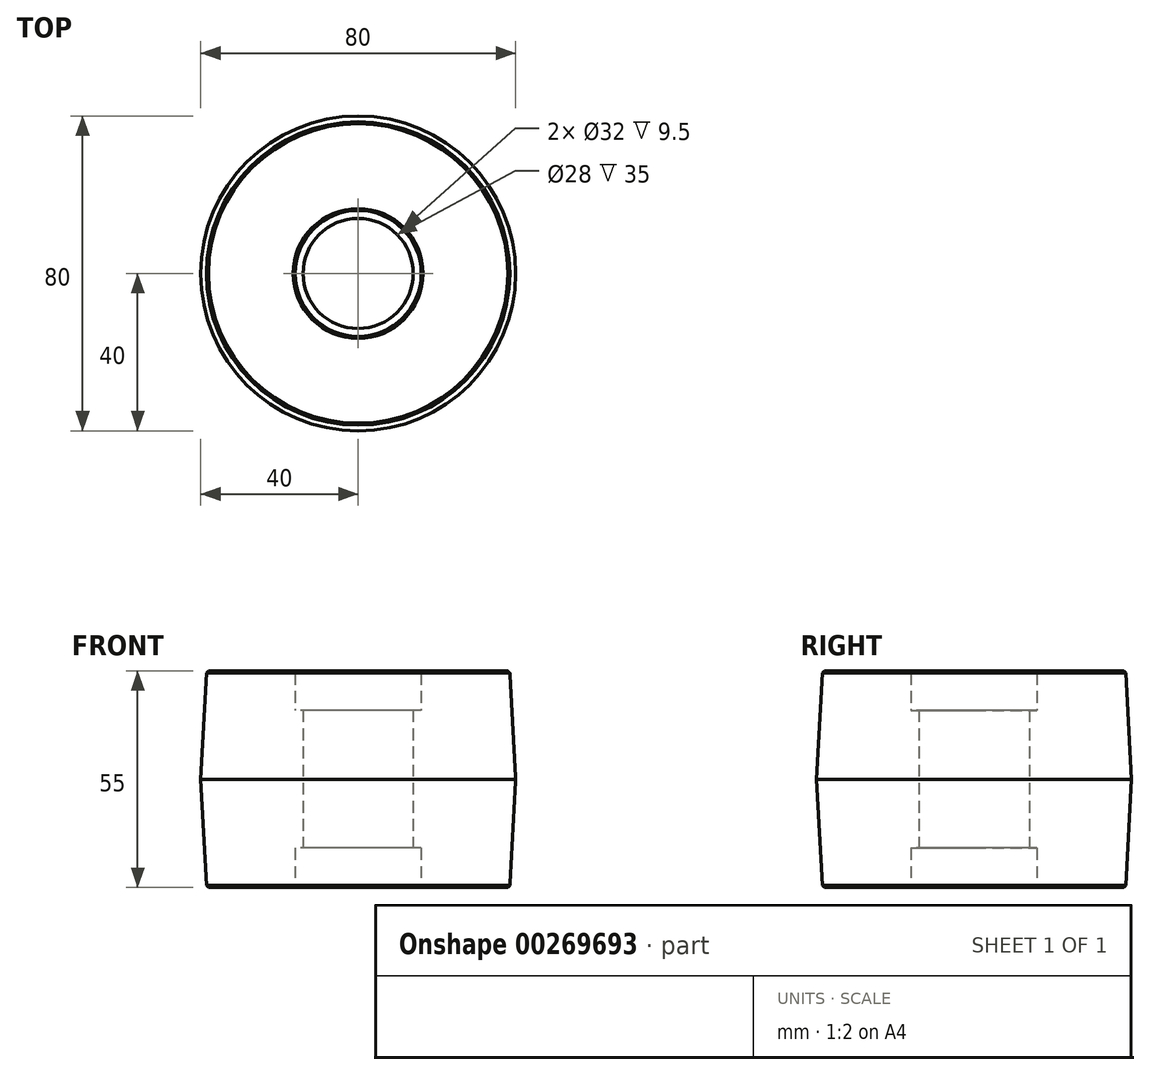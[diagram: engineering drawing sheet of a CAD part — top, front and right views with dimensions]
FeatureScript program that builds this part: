
annotation { "Feature Type Name" : "Feature", "Feature Type Description" : "" }
export const myFeature = defineFeature(function(context is Context, id is Id, definition is map)
    precondition{}
    {
        {
            var Q0;
            Q0=qCreatedBy(makeId("Top.planeOp"),FACE);
            var sketch = newSketch(context, id + "F0", { "sketchPlane" : qUnion([Q0])});
            skCircle(sketch, "E0", {"center": v(0, 0) * mm, "radius": 14 * mm});
            skCircle(sketch, "E1", {"center": v(0, 0) * mm, "radius": 16 * mm});
            skSolve(sketch);
        }
        {
            var Q0;
            Q0 = qSketchRegion(id + "F0", true);
            extrude(context, id + "F1", {"entities" : qUnion([Q0]), "endBound" : BoundingType.SYMMETRIC, "depth" : 35 * mm});
        }
        {
            var Q0;
            Q0=qCreatedBy(makeId("Top.planeOp"),FACE);
            var sketch = newSketch(context, id + "F2", { "sketchPlane" : qUnion([Q0])});
            skCircle(sketch, "E2", {"center": v(0, 0) * mm, "radius": 40 * mm});
            skCircle(sketch, "E3", {"center": v(0, 0) * mm, "radius": 16 * mm});
            skSolve(sketch);
        }
        {
            var Q0;
            Q0 = qSketchRegion(id + "F2", true);
            extrude(context, id + "F3", {"entities" : qUnion([Q0]), "operationType" : NewBodyOperationType.ADD, "endBound" : BoundingType.SYMMETRIC, "depth" : 55 * mm});
        }
        {
            var Q0;
            Q0=makeQuery(id+"F3.opExtrude","CAP_EDGE",EDGE,{"disambiguationData":[OSD([sQuery(id+"F2.wireOp",EDGE,"E2")])],"isStart":false});
            var Q1;
            Q1=makeQuery(id+"F3.opExtrude","CAP_EDGE",EDGE,{"disambiguationData":[OSD([sQuery(id+"F2.wireOp",EDGE,"E2")])],"isStart":true});
            chamfer(context, id + "F4", {"entities" : qUnion([Q0, Q1]), "chamferType" : ChamferType.TWO_OFFSETS, "width1" : 1.5 * mm, "oppositeDirection" : false, "width2" : 27.5 * mm, "tangentPropagation" : true});
        }
        {
            var Q0;
            {var subQ0=sQuery(id+"F2.wireOp",EDGE,"E2");Q0=makeQuery(id+"F4.opChamfer","BLEND_EDGE",EDGE,{"blendedFrom":[makeQuery(id+"F3.opExtrude","CAP_EDGE",EDGE,{"disambiguationData":[OSD([subQ0])],"isStart":false}),makeQuery(id+"F3.opExtrude","CAP_FACE",FACE,{"disambiguationData":[OSD([subQ0,sQuery(id+"F2.wireOp",EDGE,"E3")])],"isStart":false})],"blendedInto":[makeQuery(id+"F3.opExtrude","CAP_FACE",FACE,{"disambiguationData":[OSD([subQ0,sQuery(id+"F2.wireOp",EDGE,"E3")])],"isStart":false})]});}
            var Q1;
            Q1=makeQuery(id+"F3.opExtrude","CAP_EDGE",EDGE,{"disambiguationData":[OSD([sQuery(id+"F2.wireOp",EDGE,"E3")])],"isStart":false});
            var Q2;
            {var subQ0=sQuery(id+"F2.wireOp",EDGE,"E2");Q2=makeQuery(id+"F4.opChamfer","BLEND_EDGE",EDGE,{"blendedFrom":[makeQuery(id+"F3.opExtrude","CAP_EDGE",EDGE,{"disambiguationData":[OSD([subQ0])],"isStart":true}),makeQuery(id+"F3.opExtrude","CAP_FACE",FACE,{"disambiguationData":[OSD([subQ0,sQuery(id+"F2.wireOp",EDGE,"E3")])],"isStart":true})],"blendedInto":[makeQuery(id+"F3.opExtrude","CAP_FACE",FACE,{"disambiguationData":[OSD([subQ0,sQuery(id+"F2.wireOp",EDGE,"E3")])],"isStart":true})]});}
            var Q3;
            Q3=makeQuery(id+"F3.opExtrude","CAP_EDGE",EDGE,{"disambiguationData":[OSD([sQuery(id+"F2.wireOp",EDGE,"E3")])],"isStart":true});
            chamfer(context, id + "F5", {"entities" : qUnion([Q0, Q1, Q2, Q3]), "width" : 0.5 * mm, "tangentPropagation" : true});
        }
    });
